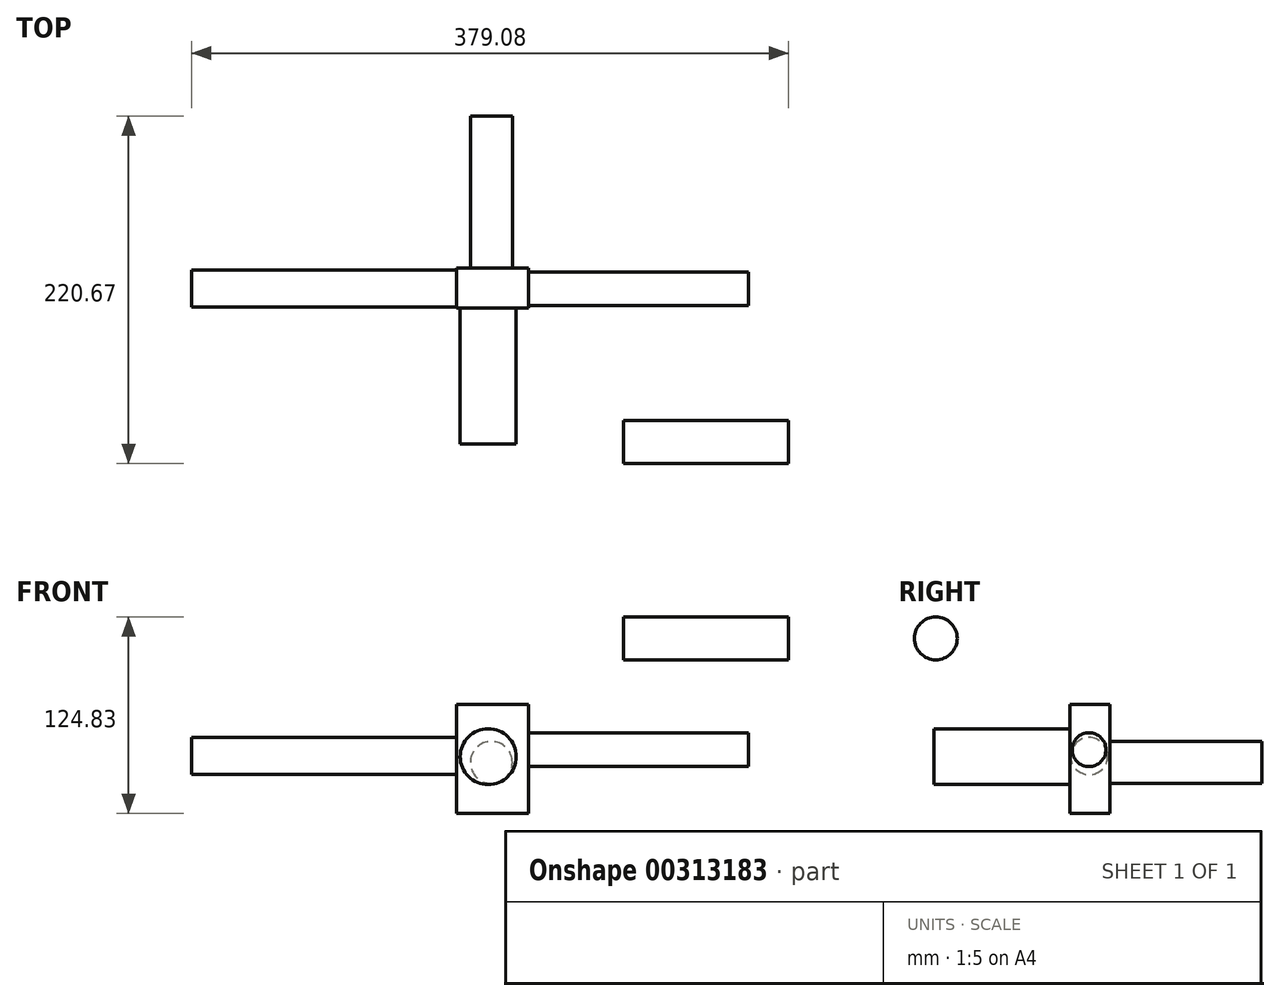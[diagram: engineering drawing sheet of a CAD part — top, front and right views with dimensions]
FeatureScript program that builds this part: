
annotation { "Feature Type Name" : "Feature", "Feature Type Description" : "" }
export const myFeature = defineFeature(function(context is Context, id is Id, definition is map)
    precondition{}
    {
        {
            var Q0;
            Q0=qCreatedBy(makeId("Front.planeOp"),FACE);
            var sketch = newSketch(context, id + "F0", { "sketchPlane" : qUnion([Q0])});
            skLineSegment(sketch, "E0.bottom", {"start": v(-106.03, 0) * mm, "end": v(-60.06, 0) * mm});
            skLineSegment(sketch, "E0.top", {"start": v(-106.03, -69.13) * mm, "end": v(-60.06, -69.13) * mm});
            skLineSegment(sketch, "E0.left", {"start": v(-106.03, 0) * mm, "end": v(-106.03, -69.13) * mm});
            skLineSegment(sketch, "E0.right", {"start": v(-60.06, 0) * mm, "end": v(-60.06, -69.13) * mm});
            skCircle(sketch, "E1", {"center": v(-85.8, -33.05) * mm, "radius": 17.77 * mm});
            skSolve(sketch);
        }
        {
            var Q0;
            Q0=makeQuery(id+"F0.imprint","IMPRINT",FACE,{"disambiguationData":[TD([[makeQuery(id+"F0.imprint","IMPRINT",EDGE,{"derivedFrom":sQuery(id+"F0.wireOp",EDGE,"E0.bottom")}),-1.0]])]});
            extrude(context, id + "F1", {"entities" : qUnion([Q0]), "depth" : 25.4 * mm});
        }
        {
            var Q0;
            Q0=qCreatedBy(makeId("Right.planeOp"),FACE);
            var sketch = newSketch(context, id + "F2", { "sketchPlane" : qUnion([Q0])});
            skCircle(sketch, "E2", {"center": v(-110.54, 42.09) * mm, "radius": 13.61 * mm});
            skSolve(sketch);
        }
        {
            var Q0;
            Q0 = qSketchRegion(id + "F2", true);
            extrude(context, id + "F3", {"entities" : qUnion([Q0]), "depth" : 104.9 * mm});
        }
        {
            var Q0;
            Q0=makeQuery(id+"F1.opExtrude","SWEPT_FACE",FACE,{"disambiguationData":[OSD([sQuery(id+"F0.wireOp",EDGE,"E0.right")])]});
            var sketch = newSketch(context, id + "F4", { "sketchPlane" : qUnion([Q0])});
            skCircle(sketch, "E3", {"center": v(-13.2, -28.61) * mm, "radius": 10.74 * mm});
            skSolve(sketch);
        }
        {
            var Q0;
            Q0 = qSketchRegion(id + "F4", true);
            extrude(context, id + "F5", {"entities" : qUnion([Q0]), "operationType" : NewBodyOperationType.ADD, "depth" : 139.45 * mm});
        }
        {
            var Q0;
            Q0=makeQuery(id+"F1.opExtrude","CAP_FACE",FACE,{"disambiguationData":[OSD([sQuery(id+"F0.wireOp",EDGE,"E0.bottom"),sQuery(id+"F0.wireOp",EDGE,"E0.top"),sQuery(id+"F0.wireOp",EDGE,"E0.left"),sQuery(id+"F0.wireOp",EDGE,"E0.right"),sQuery(id+"F0.wireOp",EDGE,"E1")])],"isStart":true});
            var sketch = newSketch(context, id + "F6", { "sketchPlane" : qUnion([Q0])});
            skCircle(sketch, "E4", {"center": v(85.8, -33.05) * mm, "radius": 18.11 * mm});
            skCircle(sketch, "E5", {"center": v(85.8, -33.05) * mm, "radius": 18.56 * mm});
            skSolve(sketch);
        }
        {
            var Q0;
            Q0=makeQuery(id+"F6.imprint","IMPRINT",FACE,{"disambiguationData":[TD([[makeQuery(id+"F6.imprint","IMPRINT",EDGE,{"derivedFrom":makeQuery(id+"F1.opExtrude","CAP_EDGE",EDGE,{"disambiguationData":[OSD([sQuery(id+"F0.wireOp",EDGE,"E1")])],"isStart":true})}),-1.0]])]});
            extrude(context, id + "F7", {"entities" : qUnion([Q0]), "operationType" : NewBodyOperationType.ADD, "oppositeDirection" : true, "depth" : 111.76 * mm});
        }
        {
            var Q0;
            {var subQ0=sQuery(id+"F0.wireOp",EDGE,"E1");Q0=makeQuery(id+"F7.boolean.opBoolean","MERGE",FACE,{"derivedFrom":[makeQuery(id+"F1.opExtrude","CAP_FACE",FACE,{"disambiguationData":[OSD([sQuery(id+"F0.wireOp",EDGE,"E0.bottom"),sQuery(id+"F0.wireOp",EDGE,"E0.top"),sQuery(id+"F0.wireOp",EDGE,"E0.left"),sQuery(id+"F0.wireOp",EDGE,"E0.right"),subQ0])],"isStart":true}),makeQuery(id+"F7.opExtrude","CAP_FACE",FACE,{"disambiguationData":[OSD([subQ0])],"isStart":true})]});}
            var sketch = newSketch(context, id + "F8", { "sketchPlane" : qUnion([Q0])});
            skCircle(sketch, "E6", {"center": v(83.8, -36.76) * mm, "radius": 13.35 * mm});
            skSolve(sketch);
        }
        {
            var Q0;
            Q0=makeQuery(id+"F8.imprint","IMPRINT",FACE,{"disambiguationData":[TD([[makeQuery(id+"F8.imprint","IMPRINT",EDGE,{"derivedFrom":sQuery(id+"F8.wireOp",EDGE,"E6")}),1.0]])]});
            extrude(context, id + "F9", {"entities" : qUnion([Q0]), "operationType" : NewBodyOperationType.ADD, "depth" : 96.52 * mm});
        }
        {
            var Q0;
            Q0=makeQuery(id+"F1.opExtrude","SWEPT_FACE",FACE,{"disambiguationData":[OSD([sQuery(id+"F0.wireOp",EDGE,"E0.left")])]});
            var sketch = newSketch(context, id + "F10", { "sketchPlane" : qUnion([Q0])});
            skCircle(sketch, "E7", {"center": v(13.14, -32.65) * mm, "radius": 11.78 * mm});
            skSolve(sketch);
        }
        {
            var Q0;
            Q0 = qSketchRegion(id + "F10", true);
            extrude(context, id + "F11", {"entities" : qUnion([Q0]), "operationType" : NewBodyOperationType.ADD, "depth" : 168.15 * mm});
        }
    });
